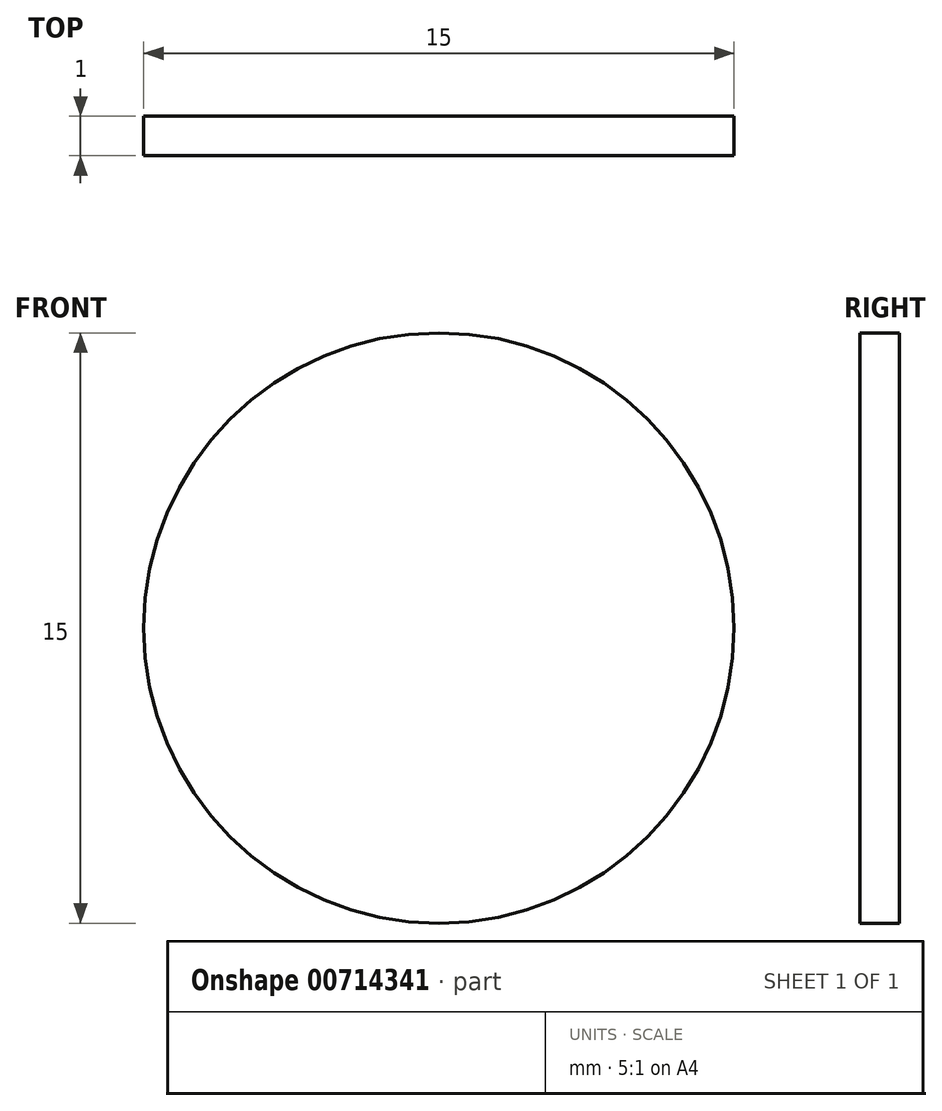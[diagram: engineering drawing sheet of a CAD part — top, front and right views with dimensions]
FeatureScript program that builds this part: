
annotation { "Feature Type Name" : "Feature", "Feature Type Description" : "" }
export const myFeature = defineFeature(function(context is Context, id is Id, definition is map)
    precondition{}
    {
        {
            var Q0;
            Q0=qCreatedBy(makeId("Front.planeOp"),FACE);
            var sketch = newSketch(context, id + "F0", { "sketchPlane" : qUnion([Q0])});
            skCircle(sketch, "E0", {"center": v(0, 0) * mm, "radius": 7.5 * mm});
            skSolve(sketch);
        }
        {
            var Q0;
            Q0=qSketchRegion(id+"F0",true);
            extrude(context, id + "F1", {"entities" : qUnion([Q0]), "depth" : 1 * mm, "offsetDistance" : 25 * mm});
        }
    });
